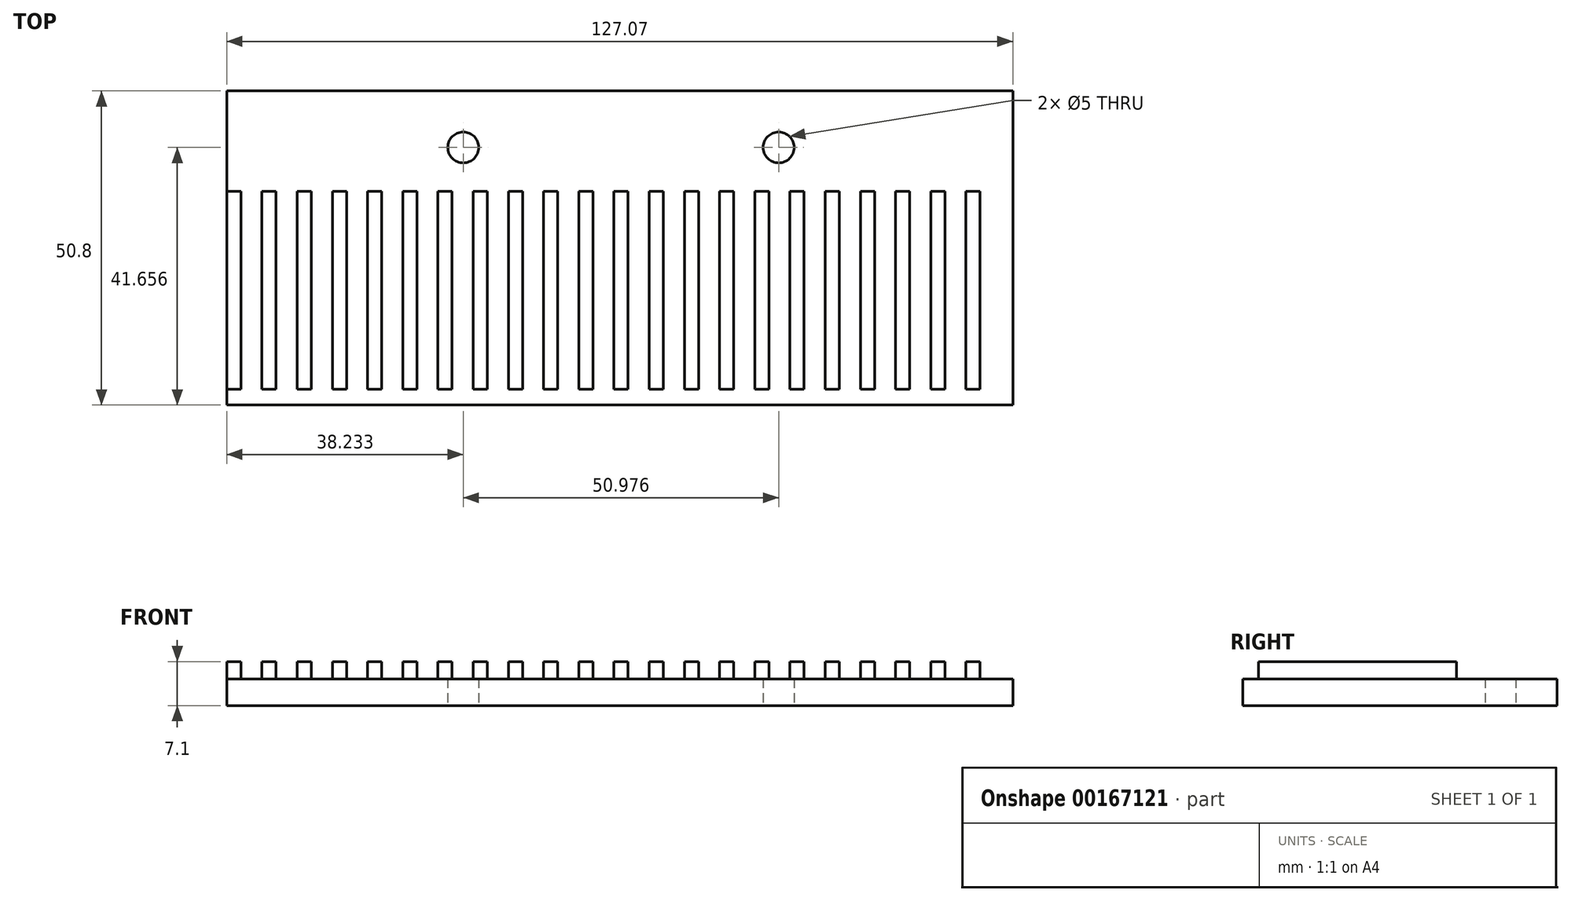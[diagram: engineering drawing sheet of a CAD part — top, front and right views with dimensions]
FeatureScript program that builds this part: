
annotation { "Feature Type Name" : "Feature", "Feature Type Description" : "" }
export const myFeature = defineFeature(function(context is Context, id is Id, definition is map)
    precondition{}
    {
        {
            var Q0;
            Q0=qCreatedBy(makeId("Top.planeOp"),FACE);
            var sketch = newSketch(context, id + "F0", { "sketchPlane" : qUnion([Q0])});
            skLineSegment(sketch, "E0.bottom", {"start": v(0, 0) * mm, "end": v(127.07, 0) * mm});
            skLineSegment(sketch, "E0.top", {"start": v(0, -50.8) * mm, "end": v(127.07, -50.8) * mm});
            skLineSegment(sketch, "E0.left", {"start": v(0, 0) * mm, "end": v(0, -50.8) * mm});
            skLineSegment(sketch, "E0.right", {"start": v(127.07, 0) * mm, "end": v(127.07, -50.8) * mm});
            skCircle(sketch, "E1", {"center": v(89.2, -9.14) * mm, "radius": 2.5 * mm});
            skCircle(sketch, "E2", {"center": v(38.23, -9.14) * mm, "radius": 2.5 * mm});
            skSolve(sketch);
        }
        {
            var Q0;
            Q0=makeQuery(id+"F0.imprint","IMPRINT",FACE,{"disambiguationData":[TD([[makeQuery(id+"F0.imprint","IMPRINT",EDGE,{"derivedFrom":sQuery(id+"F0.wireOp",EDGE,"E0.bottom")}),-1.0]])]});
            extrude(context, id + "F1", {"entities" : qUnion([Q0]), "depth" : 4.3 * mm});
        }
        {
            var Q0;
            Q0=makeQuery(id+"F1.opExtrude","CAP_FACE",FACE,{"disambiguationData":[OSD([sQuery(id+"F0.wireOp",EDGE,"E0.bottom"),sQuery(id+"F0.wireOp",EDGE,"E0.top"),sQuery(id+"F0.wireOp",EDGE,"E0.left"),sQuery(id+"F0.wireOp",EDGE,"E0.right"),sQuery(id+"F0.wireOp",EDGE,"E1"),sQuery(id+"F0.wireOp",EDGE,"E2")])],"isStart":false});
            var sketch = newSketch(context, id + "F2", { "sketchPlane" : qUnion([Q0])});
            skLineSegment(sketch, "E3.bottom", {"start": v(0, -16.26) * mm, "end": v(2.29, -16.26) * mm});
            skLineSegment(sketch, "E3.top", {"start": v(0, -48.26) * mm, "end": v(2.29, -48.26) * mm});
            skLineSegment(sketch, "E3.left", {"start": v(0, -16.26) * mm, "end": v(0, -48.26) * mm});
            skLineSegment(sketch, "E3.right", {"start": v(2.29, -16.26) * mm, "end": v(2.29, -48.26) * mm});
            skLineSegment(sketch, "E4.1.0.0", {"start": v(7.98, -16.26) * mm, "end": v(7.98, -48.26) * mm});
            skLineSegment(sketch, "E4.1.0.1", {"start": v(5.69, -16.26) * mm, "end": v(5.69, -48.26) * mm});
            skLineSegment(sketch, "E4.1.0.2", {"start": v(5.69, -48.26) * mm, "end": v(7.98, -48.26) * mm});
            skLineSegment(sketch, "E4.1.0.3", {"start": v(5.69, -16.26) * mm, "end": v(7.98, -16.26) * mm});
            skLineSegment(sketch, "E4.2.0.0", {"start": v(13.67, -16.26) * mm, "end": v(13.67, -48.26) * mm});
            skLineSegment(sketch, "E4.2.0.1", {"start": v(11.38, -16.26) * mm, "end": v(11.38, -48.26) * mm});
            skLineSegment(sketch, "E4.2.0.2", {"start": v(11.38, -48.26) * mm, "end": v(13.67, -48.26) * mm});
            skLineSegment(sketch, "E4.2.0.3", {"start": v(11.38, -16.26) * mm, "end": v(13.67, -16.26) * mm});
            skLineSegment(sketch, "E4.3.0.0", {"start": v(19.35, -16.26) * mm, "end": v(19.35, -48.26) * mm});
            skLineSegment(sketch, "E4.3.0.1", {"start": v(17.07, -16.26) * mm, "end": v(17.07, -48.26) * mm});
            skLineSegment(sketch, "E4.3.0.2", {"start": v(17.07, -48.26) * mm, "end": v(19.35, -48.26) * mm});
            skLineSegment(sketch, "E4.3.0.3", {"start": v(17.07, -16.26) * mm, "end": v(19.35, -16.26) * mm});
            skLineSegment(sketch, "E4.4.0.0", {"start": v(25.04, -16.26) * mm, "end": v(25.04, -48.26) * mm});
            skLineSegment(sketch, "E4.4.0.1", {"start": v(22.76, -16.26) * mm, "end": v(22.76, -48.26) * mm});
            skLineSegment(sketch, "E4.4.0.2", {"start": v(22.76, -48.26) * mm, "end": v(25.04, -48.26) * mm});
            skLineSegment(sketch, "E4.4.0.3", {"start": v(22.76, -16.26) * mm, "end": v(25.04, -16.26) * mm});
            skLineSegment(sketch, "E4.5.0.0", {"start": v(30.73, -16.26) * mm, "end": v(30.73, -48.26) * mm});
            skLineSegment(sketch, "E4.5.0.1", {"start": v(28.45, -16.26) * mm, "end": v(28.45, -48.26) * mm});
            skLineSegment(sketch, "E4.5.0.2", {"start": v(28.45, -48.26) * mm, "end": v(30.73, -48.26) * mm});
            skLineSegment(sketch, "E4.5.0.3", {"start": v(28.45, -16.26) * mm, "end": v(30.73, -16.26) * mm});
            skLineSegment(sketch, "E4.6.0.0", {"start": v(36.42, -16.26) * mm, "end": v(36.42, -48.26) * mm});
            skLineSegment(sketch, "E4.6.0.1", {"start": v(34.14, -16.26) * mm, "end": v(34.14, -48.26) * mm});
            skLineSegment(sketch, "E4.6.0.2", {"start": v(34.14, -48.26) * mm, "end": v(36.42, -48.26) * mm});
            skLineSegment(sketch, "E4.6.0.3", {"start": v(34.14, -16.26) * mm, "end": v(36.42, -16.26) * mm});
            skLineSegment(sketch, "E4.7.0.0", {"start": v(42.11, -16.26) * mm, "end": v(42.11, -48.26) * mm});
            skLineSegment(sketch, "E4.7.0.1", {"start": v(39.83, -16.26) * mm, "end": v(39.83, -48.26) * mm});
            skLineSegment(sketch, "E4.7.0.2", {"start": v(39.83, -48.26) * mm, "end": v(42.11, -48.26) * mm});
            skLineSegment(sketch, "E4.7.0.3", {"start": v(39.83, -16.26) * mm, "end": v(42.11, -16.26) * mm});
            skLineSegment(sketch, "E4.8.0.0", {"start": v(47.8, -16.26) * mm, "end": v(47.8, -48.26) * mm});
            skLineSegment(sketch, "E4.8.0.1", {"start": v(45.52, -16.26) * mm, "end": v(45.52, -48.26) * mm});
            skLineSegment(sketch, "E4.8.0.2", {"start": v(45.52, -48.26) * mm, "end": v(47.8, -48.26) * mm});
            skLineSegment(sketch, "E4.8.0.3", {"start": v(45.52, -16.26) * mm, "end": v(47.8, -16.26) * mm});
            skLineSegment(sketch, "E4.9.0.0", {"start": v(53.5, -16.26) * mm, "end": v(53.5, -48.26) * mm});
            skLineSegment(sketch, "E4.9.0.1", {"start": v(51.2, -16.26) * mm, "end": v(51.2, -48.26) * mm});
            skLineSegment(sketch, "E4.9.0.2", {"start": v(51.2, -48.26) * mm, "end": v(53.5, -48.26) * mm});
            skLineSegment(sketch, "E4.9.0.3", {"start": v(51.2, -16.26) * mm, "end": v(53.5, -16.26) * mm});
            skLineSegment(sketch, "E4.10.0.0", {"start": v(59.18, -16.26) * mm, "end": v(59.18, -48.26) * mm});
            skLineSegment(sketch, "E4.10.0.1", {"start": v(56.9, -16.26) * mm, "end": v(56.9, -48.26) * mm});
            skLineSegment(sketch, "E4.10.0.2", {"start": v(56.9, -48.26) * mm, "end": v(59.18, -48.26) * mm});
            skLineSegment(sketch, "E4.10.0.3", {"start": v(56.9, -16.26) * mm, "end": v(59.18, -16.26) * mm});
            skLineSegment(sketch, "E4.11.0.0", {"start": v(64.87, -16.26) * mm, "end": v(64.87, -48.26) * mm});
            skLineSegment(sketch, "E4.11.0.1", {"start": v(62.59, -16.26) * mm, "end": v(62.59, -48.26) * mm});
            skLineSegment(sketch, "E4.11.0.2", {"start": v(62.59, -48.26) * mm, "end": v(64.87, -48.26) * mm});
            skLineSegment(sketch, "E4.11.0.3", {"start": v(62.59, -16.26) * mm, "end": v(64.87, -16.26) * mm});
            skLineSegment(sketch, "E4.12.0.0", {"start": v(70.56, -16.26) * mm, "end": v(70.56, -48.26) * mm});
            skLineSegment(sketch, "E4.12.0.1", {"start": v(68.28, -16.26) * mm, "end": v(68.28, -48.26) * mm});
            skLineSegment(sketch, "E4.12.0.2", {"start": v(68.28, -48.26) * mm, "end": v(70.56, -48.26) * mm});
            skLineSegment(sketch, "E4.12.0.3", {"start": v(68.28, -16.26) * mm, "end": v(70.56, -16.26) * mm});
            skLineSegment(sketch, "E4.13.0.0", {"start": v(76.25, -16.26) * mm, "end": v(76.25, -48.26) * mm});
            skLineSegment(sketch, "E4.13.0.1", {"start": v(73.96, -16.26) * mm, "end": v(73.96, -48.26) * mm});
            skLineSegment(sketch, "E4.13.0.2", {"start": v(73.96, -48.26) * mm, "end": v(76.25, -48.26) * mm});
            skLineSegment(sketch, "E4.13.0.3", {"start": v(73.96, -16.26) * mm, "end": v(76.25, -16.26) * mm});
            skLineSegment(sketch, "E4.14.0.0", {"start": v(81.94, -16.26) * mm, "end": v(81.94, -48.26) * mm});
            skLineSegment(sketch, "E4.14.0.1", {"start": v(79.65, -16.26) * mm, "end": v(79.65, -48.26) * mm});
            skLineSegment(sketch, "E4.14.0.2", {"start": v(79.65, -48.26) * mm, "end": v(81.94, -48.26) * mm});
            skLineSegment(sketch, "E4.14.0.3", {"start": v(79.65, -16.26) * mm, "end": v(81.94, -16.26) * mm});
            skLineSegment(sketch, "E4.15.0.0", {"start": v(87.63, -16.26) * mm, "end": v(87.63, -48.26) * mm});
            skLineSegment(sketch, "E4.15.0.1", {"start": v(85.34, -16.26) * mm, "end": v(85.34, -48.26) * mm});
            skLineSegment(sketch, "E4.15.0.2", {"start": v(85.34, -48.26) * mm, "end": v(87.63, -48.26) * mm});
            skLineSegment(sketch, "E4.15.0.3", {"start": v(85.34, -16.26) * mm, "end": v(87.63, -16.26) * mm});
            skLineSegment(sketch, "E4.16.0.0", {"start": v(93.32, -16.26) * mm, "end": v(93.32, -48.26) * mm});
            skLineSegment(sketch, "E4.16.0.1", {"start": v(91.03, -16.26) * mm, "end": v(91.03, -48.26) * mm});
            skLineSegment(sketch, "E4.16.0.2", {"start": v(91.03, -48.26) * mm, "end": v(93.32, -48.26) * mm});
            skLineSegment(sketch, "E4.16.0.3", {"start": v(91.03, -16.26) * mm, "end": v(93.32, -16.26) * mm});
            skLineSegment(sketch, "E4.17.0.0", {"start": v(99, -16.26) * mm, "end": v(99, -48.26) * mm});
            skLineSegment(sketch, "E4.17.0.1", {"start": v(96.72, -16.26) * mm, "end": v(96.72, -48.26) * mm});
            skLineSegment(sketch, "E4.17.0.2", {"start": v(96.72, -48.26) * mm, "end": v(99, -48.26) * mm});
            skLineSegment(sketch, "E4.17.0.3", {"start": v(96.72, -16.26) * mm, "end": v(99, -16.26) * mm});
            skLineSegment(sketch, "E4.18.0.0", {"start": v(104.7, -16.26) * mm, "end": v(104.7, -48.26) * mm});
            skLineSegment(sketch, "E4.18.0.1", {"start": v(102.41, -16.26) * mm, "end": v(102.41, -48.26) * mm});
            skLineSegment(sketch, "E4.18.0.2", {"start": v(102.41, -48.26) * mm, "end": v(104.7, -48.26) * mm});
            skLineSegment(sketch, "E4.18.0.3", {"start": v(102.41, -16.26) * mm, "end": v(104.7, -16.26) * mm});
            skLineSegment(sketch, "E4.19.0.0", {"start": v(110.39, -16.26) * mm, "end": v(110.39, -48.26) * mm});
            skLineSegment(sketch, "E4.19.0.1", {"start": v(108.1, -16.26) * mm, "end": v(108.1, -48.26) * mm});
            skLineSegment(sketch, "E4.19.0.2", {"start": v(108.1, -48.26) * mm, "end": v(110.39, -48.26) * mm});
            skLineSegment(sketch, "E4.19.0.3", {"start": v(108.1, -16.26) * mm, "end": v(110.39, -16.26) * mm});
            skLineSegment(sketch, "E4.20.0.0", {"start": v(116.08, -16.26) * mm, "end": v(116.08, -48.26) * mm});
            skLineSegment(sketch, "E4.20.0.1", {"start": v(113.8, -16.26) * mm, "end": v(113.8, -48.26) * mm});
            skLineSegment(sketch, "E4.20.0.2", {"start": v(113.8, -48.26) * mm, "end": v(116.08, -48.26) * mm});
            skLineSegment(sketch, "E4.20.0.3", {"start": v(113.8, -16.26) * mm, "end": v(116.08, -16.26) * mm});
            skLineSegment(sketch, "E4.21.0.0", {"start": v(121.77, -16.26) * mm, "end": v(121.77, -48.26) * mm});
            skLineSegment(sketch, "E4.21.0.1", {"start": v(119.48, -16.26) * mm, "end": v(119.48, -48.26) * mm});
            skLineSegment(sketch, "E4.21.0.2", {"start": v(119.48, -48.26) * mm, "end": v(121.77, -48.26) * mm});
            skLineSegment(sketch, "E4.21.0.3", {"start": v(119.48, -16.26) * mm, "end": v(121.77, -16.26) * mm});
            skLineSegment(sketch, "E4.direction1", {"start": v(0, -48.26) * mm, "end": v(5.69, -48.26) * mm, "construction": true});
            skSolve(sketch);
        }
        {
            var Q0;
            Q0=qSketchRegion(id+"F2",true);
            extrude(context, id + "F3", {"entities" : qUnion([Q0]), "operationType" : NewBodyOperationType.ADD, "depth" : 2.8 * mm});
        }
    });
